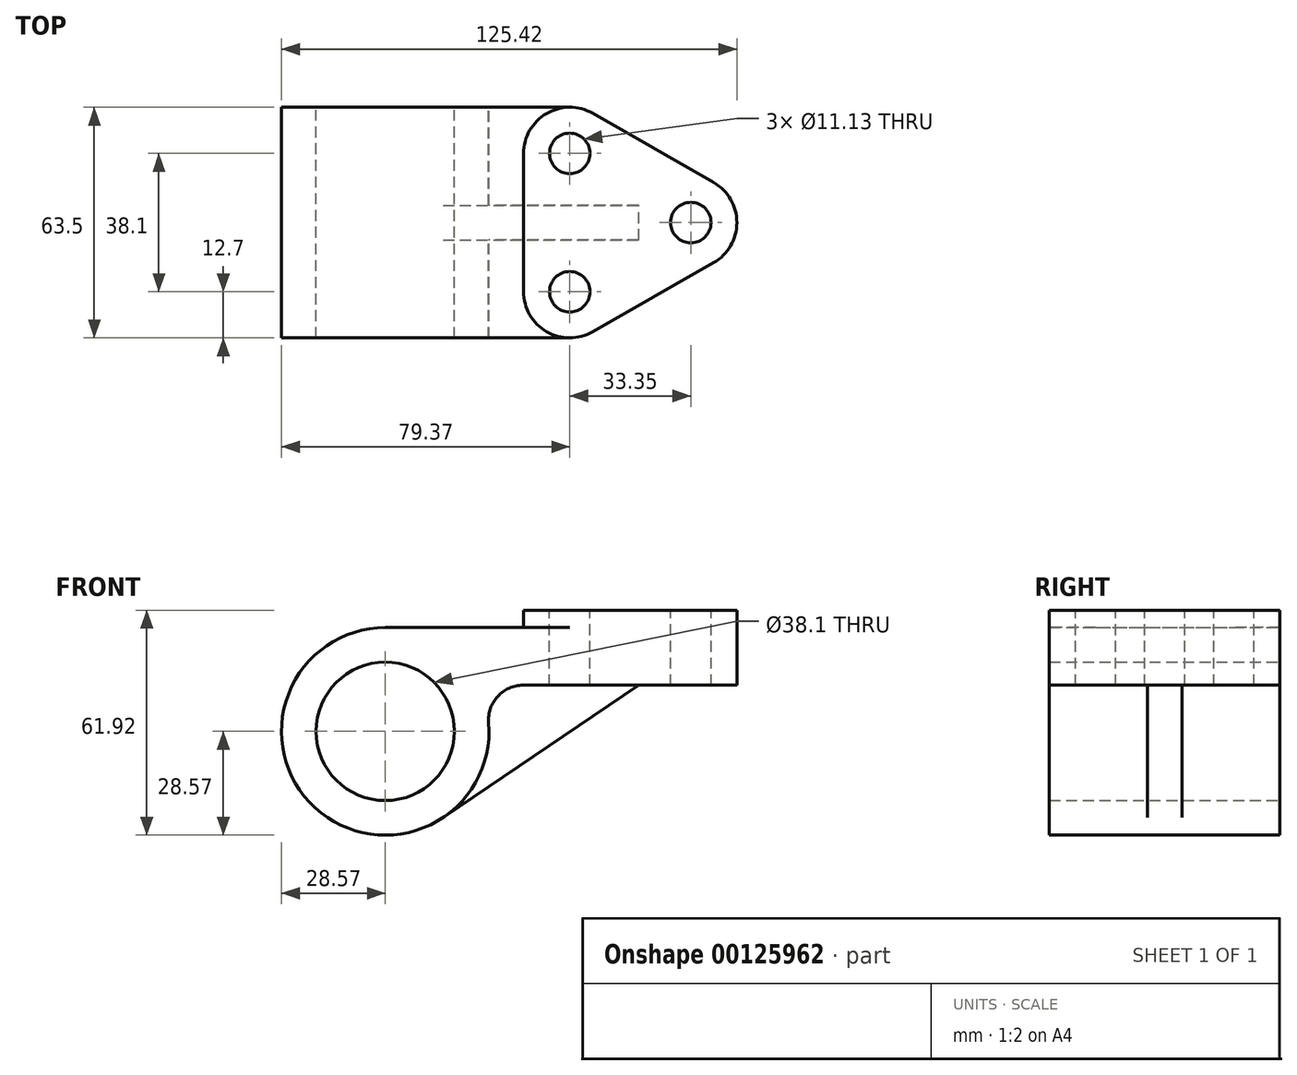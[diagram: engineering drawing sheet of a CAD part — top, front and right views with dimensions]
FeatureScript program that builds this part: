
annotation { "Feature Type Name" : "Feature", "Feature Type Description" : "" }
export const myFeature = defineFeature(function(context is Context, id is Id, definition is map)
    precondition{}
    {
        {
            var Q0;
            Q0=qCreatedBy(makeId("Front.planeOp"),FACE);
            var sketch = newSketch(context, id + "F0", { "sketchPlane" : qUnion([Q0])});
            skCircle(sketch, "E0", {"center": v(0, 0) * mm, "radius": 19.05 * mm});
            skCircle(sketch, "E1", {"center": v(0, 0) * mm, "radius": 28.58 * mm});
            skLineSegment(sketch, "E2", {"start": v(0, 28.58) * mm, "end": v(50.8, 28.58) * mm});
            skLineSegment(sketch, "E3", {"start": v(50.8, 28.58) * mm, "end": v(50.8, 12.7) * mm});
            skLineSegment(sketch, "E4", {"start": v(50.8, 12.7) * mm, "end": v(37.97, 12.7) * mm});
            skArc(sketch, "E5", {"start": v(37.97, 12.7) * mm, "mid": v(30.96, 9.62) * mm, "end": v(28.48, 2.38) * mm});
            skLineSegment(sketch, "E6", {"start": v(-63.46, 0) * mm, "end": v(65.8, 0) * mm, "construction": true});
            skLineSegment(sketch, "E7", {"start": v(0, 44.49) * mm, "end": v(0, -43.72) * mm, "construction": true});
            skLineSegment(sketch, "E8", {"start": v(0, -28.58) * mm, "end": v(38.75, -28.58) * mm, "construction": true});
            skSolve(sketch);
        }
        {
            var Q0;
            Q0=makeQuery(id+"F0.imprint","IMPRINT",FACE,{"disambiguationData":[TD([[makeQuery(id+"F0.imprint","IMPRINT",EDGE,{"derivedFrom":sQuery(id+"F0.wireOp",EDGE,"E0")}),-1.0]])]});
            var Q1;
            {var subQ0=sQuery(id+"F0.wireOp",EDGE,"E2");Q1=makeQuery(id+"F0.imprint","IMPRINT",FACE,{"disambiguationData":[TD([[makeQuery(id+"F0.imprint","IMPRINT",EDGE,{"derivedFrom":subQ0}),-1.0]])]});}
            extrude(context, id + "F1", {"entities" : qUnion([Q0, Q1]), "endBound" : BoundingType.SYMMETRIC, "depth" : 63.5 * mm});
        }
        {
            var Q0;
            Q0=makeQuery(id+"F1.opExtrude","SWEPT_FACE",FACE,{"disambiguationData":[OSD([sQuery(id+"F0.wireOp",EDGE,"E2")])]});
            var sketch = newSketch(context, id + "F2", { "sketchPlane" : qUnion([Q0])});
            skLineSegment(sketch, "E9", {"start": v(57.1, 30.08) * mm, "end": v(90.45, 11.03) * mm});
            skLineSegment(sketch, "E10", {"start": v(90.45, -11.03) * mm, "end": v(57.1, -30.08) * mm});
            skLineSegment(sketch, "E11", {"start": v(38.1, -19.05) * mm, "end": v(38.1, 19.05) * mm});
            skLineSegment(sketch, "E12", {"start": v(-54.47, 0) * mm, "end": v(178.58, 0) * mm, "construction": true});
            skPoint(sketch, "E13.visualSharp", {"position": v(109.76, 0) * mm});
            skArc(sketch, "E13.filletArc", {"start": v(90.45, -11.03) * mm, "mid": v(96.85, 0) * mm, "end": v(90.45, 11.03) * mm});
            skArc(sketch, "E14.filletArc", {"start": v(57.1, 30.08) * mm, "mid": v(44.42, 30.03) * mm, "end": v(38.1, 19.05) * mm});
            skArc(sketch, "E15.filletArc", {"start": v(38.1, -19.05) * mm, "mid": v(44.42, -30.03) * mm, "end": v(57.1, -30.08) * mm});
            skPoint(sketch, "E16", {"position": v(50.8, -31.75) * mm});
            skPoint(sketch, "E17", {"position": v(50.8, 31.75) * mm});
            skCircle(sketch, "E18", {"center": v(50.8, 19.05) * mm, "radius": 5.56 * mm});
            skCircle(sketch, "E19", {"center": v(50.8, -19.05) * mm, "radius": 5.56 * mm});
            skCircle(sketch, "E20", {"center": v(84.15, 0) * mm, "radius": 5.56 * mm});
            skSolve(sketch);
        }
        {
            var Q0;
            {var subQ13=sQuery(id+"F2.wireOp",EDGE,"E9");Q0=makeQuery(id+"F2.imprint","IMPRINT",FACE,{"disambiguationData":[TD([[makeQuery(id+"F2.imprint","IMPRINT",EDGE,{"derivedFrom":subQ13}),-1.0]])]});}
            var Q1;
            {var subQ4=sQuery(id+"F2.wireOp",EDGE,"E11");Q1=makeQuery(id+"F2.imprint","IMPRINT",FACE,{"disambiguationData":[TD([[makeQuery(id+"F2.imprint","IMPRINT",EDGE,{"derivedFrom":subQ4}),-1.0]])]});}
            extrude(context, id + "F3", {"entities" : qUnion([Q0, Q1]), "operationType" : NewBodyOperationType.ADD, "oppositeDirection" : true, "depth" : 15.88 * mm, "hasSecondDirection" : true, "secondDirectionOppositeDirection" : false, "secondDirectionDepth" : 4.78 * mm});
        }
        {
            var Q0;
            Q0=qCreatedBy(makeId("Front.planeOp"),FACE);
            var sketch = newSketch(context, id + "F4", { "sketchPlane" : qUnion([Q0])});
            skLineSegment(sketch, "E21", {"start": v(16, -23.68) * mm, "end": v(69.85, 12.7) * mm});
            skLineSegment(sketch, "E22.0", {"start": v(69.85, 12.7) * mm, "end": v(57.1, 12.7) * mm});
            skArc(sketch, "E23.0", {"start": v(16, -23.68) * mm, "mid": v(25.77, -12.34) * mm, "end": v(28.48, 2.38) * mm});
            skArc(sketch, "E24.0", {"start": v(37.97, 12.7) * mm, "mid": v(30.96, 9.62) * mm, "end": v(28.48, 2.38) * mm});
            skLineSegment(sketch, "E25.0", {"start": v(50.8, 12.7) * mm, "end": v(37.97, 12.7) * mm});
            skLineSegment(sketch, "E26.0", {"start": v(50.8, 12.7) * mm, "end": v(57.1, 12.7) * mm});
            skPoint(sketch, "E27.orphan", {"position": v(90.45, 12.7) * mm});
            skSolve(sketch);
        }
        {
            var Q0;
            Q0=makeQuery(id+"F4.imprint","IMPRINT",FACE,{"disambiguationData":[TD([[makeQuery(id+"F4.imprint","IMPRINT",EDGE,{"derivedFrom":sQuery(id+"F4.wireOp",EDGE,"E21")}),1.0]])]});
            extrude(context, id + "F5", {"entities" : qUnion([Q0]), "operationType" : NewBodyOperationType.ADD, "endBound" : BoundingType.SYMMETRIC, "depth" : 9.52 * mm});
        }
        {
            var Q0;
            Q0=makeQuery(id+"F3.boolean.opBoolean","SPLIT",FACE,{"disambiguationData":[TD([makeQuery(id+"F3.opExtrude","SWEPT_FACE",FACE,{"disambiguationData":[OSD([sQuery(id+"F2.wireOp",EDGE,"E18")])]})])],"derivedFrom":makeQuery(id+"F1.opExtrude","SWEPT_FACE",FACE,{"disambiguationData":[OSD([sQuery(id+"F0.wireOp",EDGE,"E2")])]})});
            var Q1;
            Q1=makeQuery(id+"F3.boolean.opBoolean","SPLIT",FACE,{"disambiguationData":[TD([makeQuery(id+"F3.opExtrude","SWEPT_FACE",FACE,{"disambiguationData":[OSD([sQuery(id+"F2.wireOp",EDGE,"E19")])]})])],"derivedFrom":makeQuery(id+"F1.opExtrude","SWEPT_FACE",FACE,{"disambiguationData":[OSD([sQuery(id+"F0.wireOp",EDGE,"E2")])]})});
            extrude(context, id + "F6", {"entities" : qUnion([Q0, Q1]), "operationType" : NewBodyOperationType.REMOVE, "endBound" : BoundingType.THROUGH_ALL, "oppositeDirection" : true, "depth" : 25.4 * mm});
        }
    });
